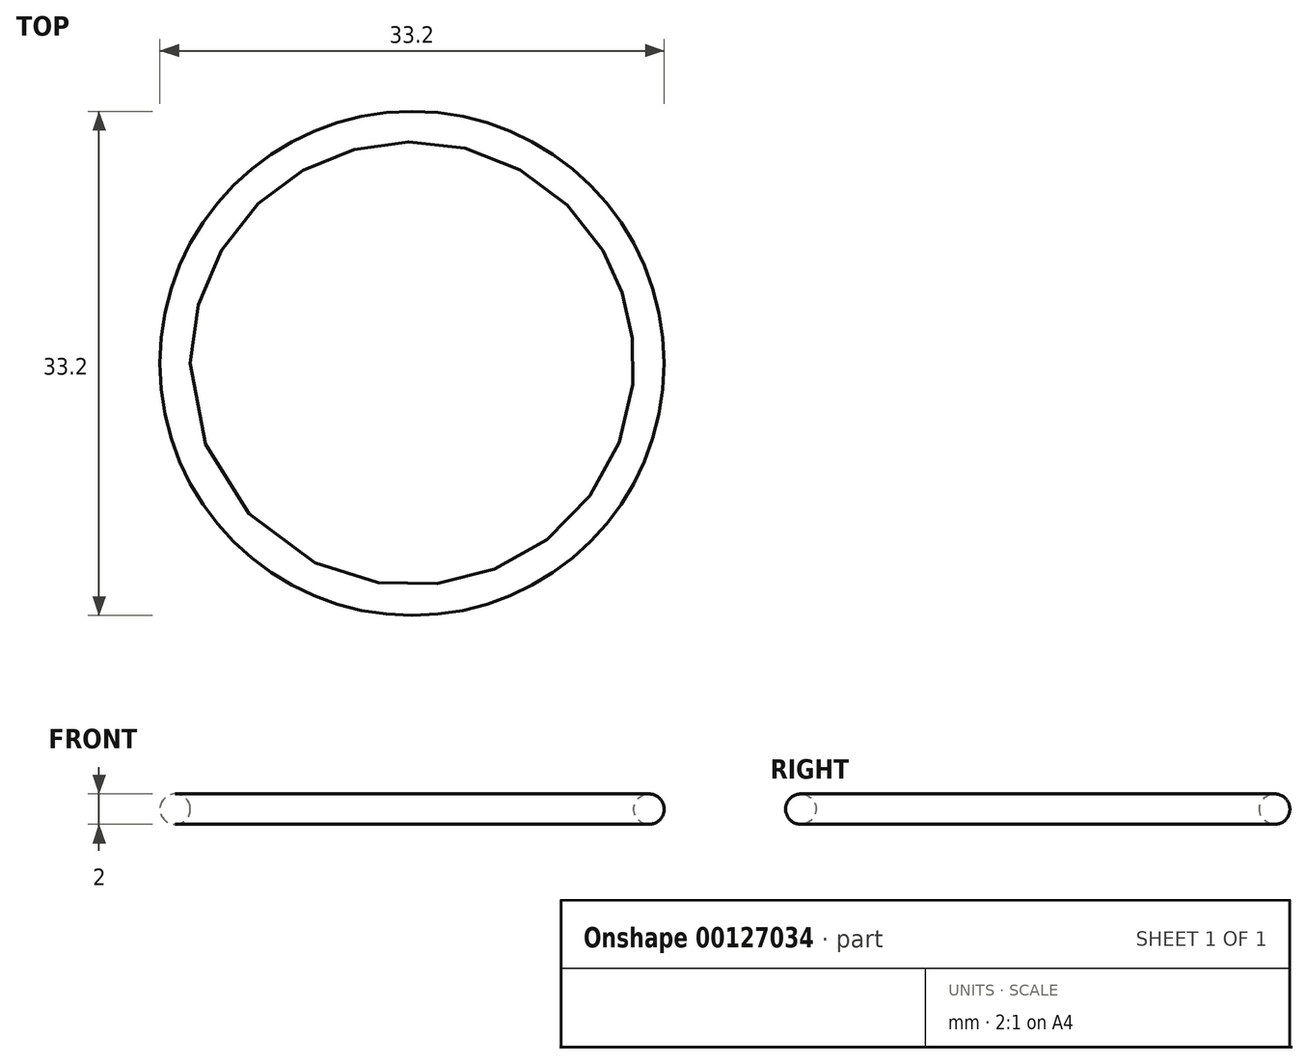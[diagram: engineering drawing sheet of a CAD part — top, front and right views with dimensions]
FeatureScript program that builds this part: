
annotation { "Feature Type Name" : "Feature", "Feature Type Description" : "" }
export const myFeature = defineFeature(function(context is Context, id is Id, definition is map)
    precondition{}
    {
        {
            var Q0;
            Q0=qCreatedBy(makeId("Front.planeOp"),FACE);
            var sketch = newSketch(context, id + "F0", { "sketchPlane" : qUnion([Q0])});
            skLineSegment(sketch, "E0", {"start": v(0, 0) * mm, "end": v(0, 4.45) * mm, "construction": true});
            skLineSegment(sketch, "E1", {"start": v(0, 0) * mm, "end": v(15.6, 0) * mm, "construction": true});
            skCircle(sketch, "E2", {"center": v(15.6, 0) * mm, "radius": 1 * mm});
            skSolve(sketch);
        }
        {
            var Q0;
            Q0=makeQuery(id+"F0.imprint","IMPRINT",FACE,{"disambiguationData":[TD([[makeQuery(id+"F0.imprint","IMPRINT",EDGE,{"derivedFrom":sQuery(id+"F0.wireOp",EDGE,"E2")}),1.0]])]});
            var Q1;
            Q1=sQuery(id+"F0.wireOp",EDGE,"E0");
            revolve(context, id + "F1", {"entities" : qUnion([Q0]), "axis" : qUnion([Q1]), "revolveType" : RevolveType.FULL});
        }
    });
